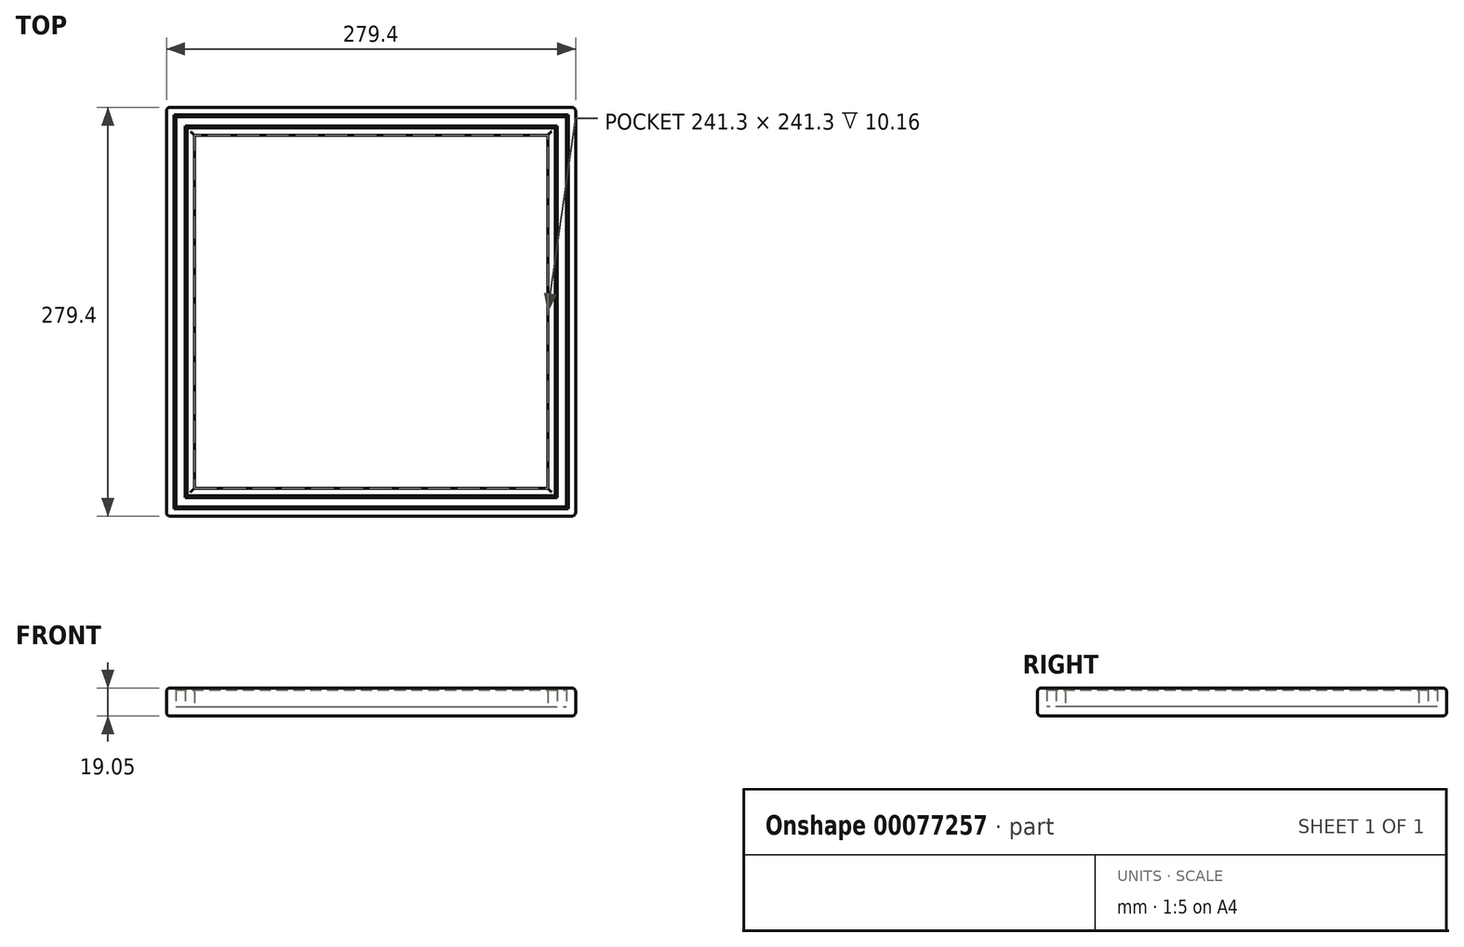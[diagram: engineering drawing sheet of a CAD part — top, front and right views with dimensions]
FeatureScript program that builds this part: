
annotation { "Feature Type Name" : "Feature", "Feature Type Description" : "" }
export const myFeature = defineFeature(function(context is Context, id is Id, definition is map)
    precondition{}
    {
        {
            var Q0;
            Q0=qCreatedBy(makeId("Top.planeOp"),FACE);
            var sketch = newSketch(context, id + "F0", { "sketchPlane" : qUnion([Q0])});
            skLineSegment(sketch, "E0.bottom", {"start": v(139.7, -139.7) * mm, "end": v(-139.7, -139.7) * mm});
            skLineSegment(sketch, "E0.top", {"start": v(139.7, 139.7) * mm, "end": v(-139.7, 139.7) * mm});
            skLineSegment(sketch, "E0.left", {"start": v(139.7, -139.7) * mm, "end": v(139.7, 139.7) * mm});
            skLineSegment(sketch, "E0.right", {"start": v(-139.7, -139.7) * mm, "end": v(-139.7, 139.7) * mm});
            skPoint(sketch, "E0.middle", {"position": v(0, 0) * mm});
            skLineSegment(sketch, "E1.bottom", {"start": v(133.35, -133.35) * mm, "end": v(-133.35, -133.35) * mm});
            skLineSegment(sketch, "E1.top", {"start": v(133.35, 133.35) * mm, "end": v(-133.35, 133.35) * mm});
            skLineSegment(sketch, "E1.left", {"start": v(133.35, -133.35) * mm, "end": v(133.35, 133.35) * mm});
            skLineSegment(sketch, "E1.right", {"start": v(-133.35, -133.35) * mm, "end": v(-133.35, 133.35) * mm});
            skLineSegment(sketch, "E2.bottom", {"start": v(127, -127) * mm, "end": v(-127, -127) * mm});
            skLineSegment(sketch, "E2.top", {"start": v(127, 127) * mm, "end": v(-127, 127) * mm});
            skLineSegment(sketch, "E2.left", {"start": v(127, -127) * mm, "end": v(127, 127) * mm});
            skLineSegment(sketch, "E2.right", {"start": v(-127, -127) * mm, "end": v(-127, 127) * mm});
            skLineSegment(sketch, "E3.bottom", {"start": v(120.65, -120.65) * mm, "end": v(-120.65, -120.65) * mm});
            skLineSegment(sketch, "E3.top", {"start": v(120.65, 120.65) * mm, "end": v(-120.65, 120.65) * mm});
            skLineSegment(sketch, "E3.left", {"start": v(120.65, -120.65) * mm, "end": v(120.65, 120.65) * mm});
            skLineSegment(sketch, "E3.right", {"start": v(-120.65, -120.65) * mm, "end": v(-120.65, 120.65) * mm});
            skSolve(sketch);
        }
        {
            var Q0;
            Q0=makeQuery(id+"F0.imprint","IMPRINT",FACE,{"disambiguationData":[TD([[makeQuery(id+"F0.imprint","IMPRINT",EDGE,{"derivedFrom":sQuery(id+"F0.wireOp",EDGE,"E3.bottom")}),-1.0]])]});
            var Q1;
            Q1=makeQuery(id+"F0.imprint","IMPRINT",FACE,{"disambiguationData":[TD([[makeQuery(id+"F0.imprint","IMPRINT",EDGE,{"derivedFrom":sQuery(id+"F0.wireOp",EDGE,"E2.bottom")}),-1.0]])]});
            var Q2;
            Q2=makeQuery(id+"F0.imprint","IMPRINT",FACE,{"disambiguationData":[TD([[makeQuery(id+"F0.imprint","IMPRINT",EDGE,{"derivedFrom":sQuery(id+"F0.wireOp",EDGE,"E1.bottom")}),-1.0]])]});
            var Q3;
            Q3=makeQuery(id+"F0.imprint","IMPRINT",FACE,{"disambiguationData":[TD([[makeQuery(id+"F0.imprint","IMPRINT",EDGE,{"derivedFrom":sQuery(id+"F0.wireOp",EDGE,"E0.bottom")}),-1.0]])]});
            extrude(context, id + "F1", {"entities" : qUnion([Q0, Q1, Q2, Q3]), "depth" : 6.35 * mm});
        }
        {
            var Q0;
            Q0=makeQuery(id+"F0.imprint","IMPRINT",FACE,{"disambiguationData":[TD([[makeQuery(id+"F0.imprint","IMPRINT",EDGE,{"derivedFrom":sQuery(id+"F0.wireOp",EDGE,"E0.bottom")}),-1.0]])]});
            var Q1;
            Q1=makeQuery(id+"F0.imprint","IMPRINT",FACE,{"disambiguationData":[TD([[makeQuery(id+"F0.imprint","IMPRINT",EDGE,{"derivedFrom":sQuery(id+"F0.wireOp",EDGE,"E2.bottom")}),-1.0]])]});
            extrude(context, id + "F2", {"entities" : qUnion([Q0, Q1]), "operationType" : NewBodyOperationType.ADD, "depth" : 19.05 * mm});
        }
        {
            var Q0;
            Q0=makeQuery(id+"F2.opExtrude","CAP_EDGE",EDGE,{"disambiguationData":[OSD([sQuery(id+"F0.wireOp",EDGE,"E2.right")])],"isStart":false});
            var Q1;
            Q1=makeQuery(id+"F2.opExtrude","CAP_EDGE",EDGE,{"disambiguationData":[OSD([sQuery(id+"F0.wireOp",EDGE,"E1.right")])],"isStart":false});
            var Q2;
            Q2=makeQuery(id+"F2.opExtrude","CAP_EDGE",EDGE,{"disambiguationData":[OSD([sQuery(id+"F0.wireOp",EDGE,"E1.top")])],"isStart":false});
            var Q3;
            Q3=makeQuery(id+"F2.opExtrude","CAP_EDGE",EDGE,{"disambiguationData":[OSD([sQuery(id+"F0.wireOp",EDGE,"E2.top")])],"isStart":false});
            var Q4;
            Q4=makeQuery(id+"F2.opExtrude","CAP_EDGE",EDGE,{"disambiguationData":[OSD([sQuery(id+"F0.wireOp",EDGE,"E1.left")])],"isStart":false});
            var Q5;
            Q5=makeQuery(id+"F2.opExtrude","CAP_EDGE",EDGE,{"disambiguationData":[OSD([sQuery(id+"F0.wireOp",EDGE,"E2.left")])],"isStart":false});
            var Q6;
            Q6=makeQuery(id+"F2.opExtrude","CAP_EDGE",EDGE,{"disambiguationData":[OSD([sQuery(id+"F0.wireOp",EDGE,"E2.bottom")])],"isStart":false});
            var Q7;
            Q7=makeQuery(id+"F2.opExtrude","CAP_EDGE",EDGE,{"disambiguationData":[OSD([sQuery(id+"F0.wireOp",EDGE,"E1.bottom")])],"isStart":false});
            chamfer(context, id + "F3", {"entities" : qUnion([Q0, Q1, Q2, Q3, Q4, Q5, Q6, Q7]), "width" : 1.27 * mm, "tangentPropagation" : true});
        }
        {
            var Q0;
            Q0=makeQuery(id+"F2.opExtrude","CAP_EDGE",EDGE,{"disambiguationData":[OSD([sQuery(id+"F0.wireOp",EDGE,"E0.right")])],"isStart":false});
            var Q1;
            Q1=makeQuery(id+"F2.opExtrude","CAP_EDGE",EDGE,{"disambiguationData":[OSD([sQuery(id+"F0.wireOp",EDGE,"E0.top")])],"isStart":false});
            var Q2;
            Q2=makeQuery(id+"F2.opExtrude","CAP_EDGE",EDGE,{"disambiguationData":[OSD([sQuery(id+"F0.wireOp",EDGE,"E0.left")])],"isStart":false});
            var Q3;
            Q3=makeQuery(id+"F2.opExtrude","CAP_EDGE",EDGE,{"disambiguationData":[OSD([sQuery(id+"F0.wireOp",EDGE,"E0.bottom")])],"isStart":false});
            var Q4;
            Q4=makeQuery(id+"F2.opExtrude","CAP_EDGE",EDGE,{"disambiguationData":[OSD([sQuery(id+"F0.wireOp",EDGE,"E3.right")])],"isStart":false});
            var Q5;
            Q5=makeQuery(id+"F2.opExtrude","CAP_EDGE",EDGE,{"disambiguationData":[OSD([sQuery(id+"F0.wireOp",EDGE,"E3.bottom")])],"isStart":false});
            var Q6;
            Q6=makeQuery(id+"F2.opExtrude","CAP_EDGE",EDGE,{"disambiguationData":[OSD([sQuery(id+"F0.wireOp",EDGE,"E3.left")])],"isStart":false});
            var Q7;
            Q7=makeQuery(id+"F2.opExtrude","CAP_EDGE",EDGE,{"disambiguationData":[OSD([sQuery(id+"F0.wireOp",EDGE,"E3.top")])],"isStart":false});
            fillet(context, id + "F4", {"entities" : qUnion([Q0, Q1, Q2, Q3, Q4, Q5, Q6, Q7]), "radius" : 2.54 * mm, "tangentPropagation" : true, "allowEdgeOverflow" : false});
        }
        {
            var Q0;
            Q0=makeQuery(id+"F1.opExtrude","CAP_EDGE",EDGE,{"disambiguationData":[OSD([sQuery(id+"F0.wireOp",EDGE,"E0.top")])],"isStart":true});
            var Q1;
            Q1=makeQuery(id+"F1.opExtrude","CAP_EDGE",EDGE,{"disambiguationData":[OSD([sQuery(id+"F0.wireOp",EDGE,"E0.right")])],"isStart":true});
            var Q2;
            Q2=makeQuery(id+"F1.opExtrude","CAP_EDGE",EDGE,{"disambiguationData":[OSD([sQuery(id+"F0.wireOp",EDGE,"E0.bottom")])],"isStart":true});
            var Q3;
            Q3=makeQuery(id+"F1.opExtrude","CAP_EDGE",EDGE,{"disambiguationData":[OSD([sQuery(id+"F0.wireOp",EDGE,"E0.left")])],"isStart":true});
            var Q4;
            {var subQ0=sQuery(id+"F0.wireOp",EDGE,"E0.left");var subQ1=sQuery(id+"F0.wireOp",EDGE,"E0.top");Q4=makeQuery(id+"F2.boolean.opBoolean","MERGE",EDGE,{"derivedFrom":[makeQuery(id+"F1.opExtrude","SWEPT_EDGE",EDGE,{"disambiguationData":[OSD([subQ1,subQ0])]}),makeQuery(id+"F2.opExtrude","SWEPT_EDGE",EDGE,{"disambiguationData":[OSD([subQ1,subQ0])]})]});}
            var Q5;
            {var subQ0=sQuery(id+"F0.wireOp",EDGE,"E0.right");var subQ1=sQuery(id+"F0.wireOp",EDGE,"E0.top");Q5=makeQuery(id+"F2.boolean.opBoolean","MERGE",EDGE,{"derivedFrom":[makeQuery(id+"F1.opExtrude","SWEPT_EDGE",EDGE,{"disambiguationData":[OSD([subQ1,subQ0])]}),makeQuery(id+"F2.opExtrude","SWEPT_EDGE",EDGE,{"disambiguationData":[OSD([subQ1,subQ0])]})]});}
            var Q6;
            {var subQ0=sQuery(id+"F0.wireOp",EDGE,"E0.right");var subQ1=sQuery(id+"F0.wireOp",EDGE,"E0.bottom");Q6=makeQuery(id+"F2.boolean.opBoolean","MERGE",EDGE,{"derivedFrom":[makeQuery(id+"F1.opExtrude","SWEPT_EDGE",EDGE,{"disambiguationData":[OSD([subQ1,subQ0])]}),makeQuery(id+"F2.opExtrude","SWEPT_EDGE",EDGE,{"disambiguationData":[OSD([subQ1,subQ0])]})]});}
            var Q7;
            {var subQ0=sQuery(id+"F0.wireOp",EDGE,"E0.left");var subQ1=sQuery(id+"F0.wireOp",EDGE,"E0.bottom");Q7=makeQuery(id+"F2.boolean.opBoolean","MERGE",EDGE,{"derivedFrom":[makeQuery(id+"F1.opExtrude","SWEPT_EDGE",EDGE,{"disambiguationData":[OSD([subQ1,subQ0])]}),makeQuery(id+"F2.opExtrude","SWEPT_EDGE",EDGE,{"disambiguationData":[OSD([subQ1,subQ0])]})]});}
            fillet(context, id + "F5", {"entities" : qUnion([Q0, Q1, Q2, Q3, Q4, Q5, Q6, Q7]), "radius" : 2.54 * mm, "tangentPropagation" : true, "allowEdgeOverflow" : false});
        }
    });
